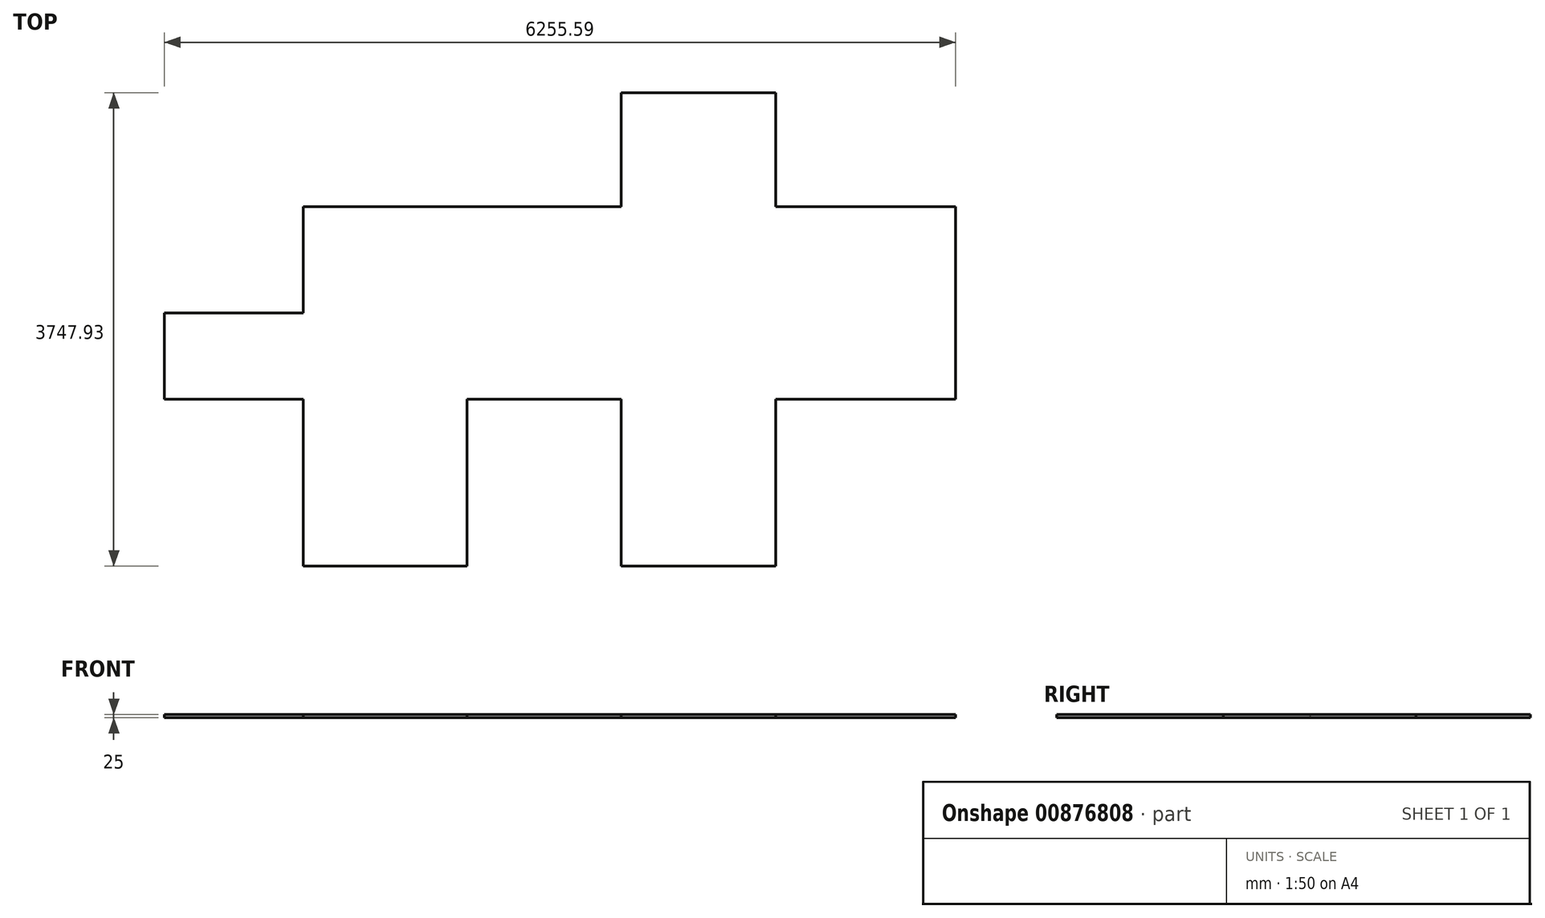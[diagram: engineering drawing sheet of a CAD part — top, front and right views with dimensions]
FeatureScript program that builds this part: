
annotation { "Feature Type Name" : "Feature", "Feature Type Description" : "" }
export const myFeature = defineFeature(function(context is Context, id is Id, definition is map)
    precondition{}
    {
        {
            var Q0;
            Q0=qCreatedBy(makeId("Top.planeOp"),FACE);
            var sketch = newSketch(context, id + "F0", { "sketchPlane" : qUnion([Q0])});
            skLineSegment(sketch, "E0", {"start": v(0, 0) * mm, "end": v(-1422, 0) * mm});
            skLineSegment(sketch, "E1", {"start": v(0, 0) * mm, "end": v(0, -1524) * mm});
            skLineSegment(sketch, "E2", {"start": v(0, -1524) * mm, "end": v(-1422, -1524) * mm});
            skLineSegment(sketch, "E3", {"start": v(-1422, -1524) * mm, "end": v(-1422, -2844) * mm});
            skLineSegment(sketch, "E4", {"start": v(-2642, -1524) * mm, "end": v(-2642, -2844) * mm});
            skLineSegment(sketch, "E5", {"start": v(-2642, -1524) * mm, "end": v(-3862, -1524) * mm});
            skLineSegment(sketch, "E6", {"start": v(-2642, -2844) * mm, "end": v(-1422, -2844) * mm});
            skLineSegment(sketch, "E7", {"start": v(-2642, 0) * mm, "end": v(-4061.8, 0) * mm});
            skLineSegment(sketch, "E8", {"start": v(-2642, 0) * mm, "end": v(-2642, 903.93) * mm});
            skLineSegment(sketch, "E9", {"start": v(-1422, 0) * mm, "end": v(-1422, 903.93) * mm});
            skLineSegment(sketch, "E10", {"start": v(-1422, 903.93) * mm, "end": v(-2642, 903.93) * mm});
            skLineSegment(sketch, "E11", {"start": v(-3862, -1524) * mm, "end": v(-3862, -2844) * mm});
            skLineSegment(sketch, "E12", {"start": v(-3862, -2844) * mm, "end": v(-5157.65, -2844) * mm});
            skLineSegment(sketch, "E13", {"start": v(-5157.65, -2844) * mm, "end": v(-5157.65, -1524) * mm});
            skLineSegment(sketch, "E14", {"start": v(-5157.65, -1524) * mm, "end": v(-6255.6, -1524) * mm});
            skLineSegment(sketch, "E15", {"start": v(-6255.6, -1524) * mm, "end": v(-6255.6, -838.58) * mm});
            skLineSegment(sketch, "E16", {"start": v(-6255.6, -838.58) * mm, "end": v(-5157.65, -838.58) * mm});
            skLineSegment(sketch, "E17", {"start": v(-5157.65, -838.58) * mm, "end": v(-5157.65, 0) * mm});
            skLineSegment(sketch, "E18", {"start": v(-5157.65, 0) * mm, "end": v(-4061.8, 0) * mm});
            skSolve(sketch);
        }
        {
            var Q0;
            Q0 = qSketchRegion(id + "F0", true);
            extrude(context, id + "F1", {"entities" : qUnion([Q0]), "depth" : 25 * mm, "offsetDistance" : 25 * mm});
        }
    });
